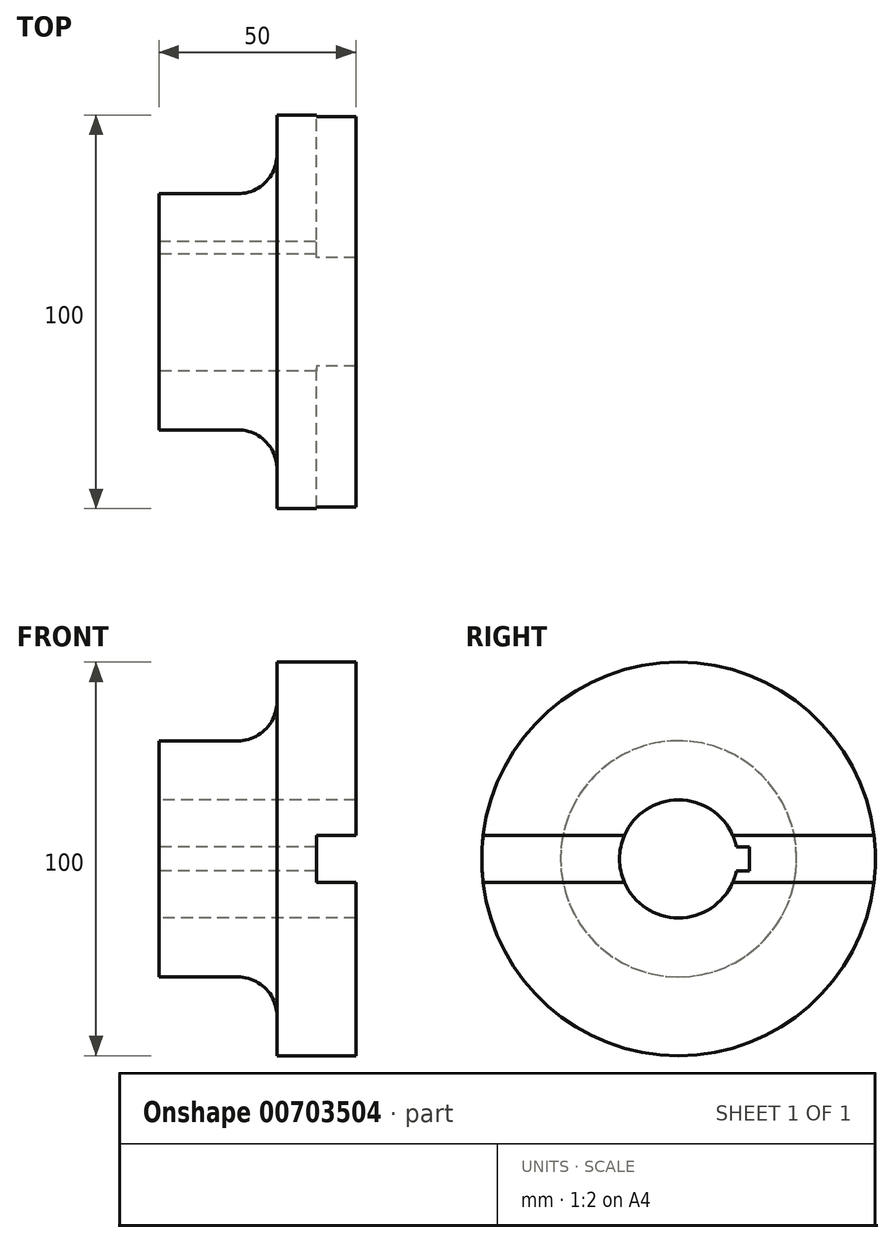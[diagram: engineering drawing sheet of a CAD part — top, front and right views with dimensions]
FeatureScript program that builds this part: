
annotation { "Feature Type Name" : "Feature", "Feature Type Description" : "" }
export const myFeature = defineFeature(function(context is Context, id is Id, definition is map)
    precondition{}
    {
        {
            var Q0;
            Q0=qCreatedBy(makeId("Top.planeOp"),FACE);
            var sketch = newSketch(context, id + "F0", { "sketchPlane" : qUnion([Q0])});
            skLineSegment(sketch, "E0", {"start": v(0, 0) * mm, "end": v(0, 50) * mm});
            skLineSegment(sketch, "E1", {"start": v(0, 50) * mm, "end": v(-20, 50) * mm});
            skLineSegment(sketch, "E2", {"start": v(-20, 50) * mm, "end": v(-20, 30) * mm});
            skLineSegment(sketch, "E3", {"start": v(-20, 30) * mm, "end": v(-50, 30) * mm});
            skLineSegment(sketch, "E4", {"start": v(-50, 30) * mm, "end": v(-50, 0) * mm});
            skLineSegment(sketch, "E5", {"start": v(-50, 0) * mm, "end": v(0, 0) * mm});
            skSolve(sketch);
        }
        {
            var Q0;
            Q0 = qSketchRegion(id + "F0", true);
            var Q1;
            Q1=sQuery(id+"F0.wireOp",EDGE,"E5");
            revolve(context, id + "F1", {"surfaceOperationType" : NewSurfaceOperationType.NEW, "entities" : qUnion([Q0]), "axis" : qUnion([Q1]), "revolveType" : RevolveType.FULL});
        }
        {
            var Q0;
            Q0=makeQuery(id+"F1.opRevolve","SWEPT_FACE",FACE,{"disambiguationData":[OSD([sQuery(id+"F0.wireOp",EDGE,"E0")])]});
            var sketch = newSketch(context, id + "F2", { "sketchPlane" : qUnion([Q0])});
            skLineSegment(sketch, "E6.bottom", {"start": v(-50, 6) * mm, "end": v(50, 6) * mm});
            skLineSegment(sketch, "E6.top", {"start": v(-50, -6) * mm, "end": v(50, -6) * mm});
            skLineSegment(sketch, "E6.left", {"start": v(-50, 6) * mm, "end": v(-50, -6) * mm});
            skLineSegment(sketch, "E6.right", {"start": v(50, 6) * mm, "end": v(50, -6) * mm});
            skPoint(sketch, "E6.middle", {"position": v(0, 0) * mm});
            skSolve(sketch);
        }
        {
            var Q0;
            {var subQ0=sQuery(id+"F2.wireOp",EDGE,"E6.bottom");var subQ1=makeQuery(id+"F1.opRevolve","SWEPT_EDGE",EDGE,{"disambiguationData":[OSD([sQuery(id+"F0.wireOp",EDGE,"E0"),sQuery(id+"F0.wireOp",EDGE,"E1")])]});var subQ4=makeQuery(id+"F2.imprint","INTERSECT",VERTEX,{"disambiguationData":[OD(0.0)],"derivedFrom":[subQ1,subQ0]});Q0=makeQuery(id+"F2.imprint","IMPRINT",FACE,{"disambiguationData":[TD([[makeQuery(id+"F2.imprint","IMPRINT",EDGE,{"disambiguationData":[TD([[subQ4,-1.0]])],"derivedFrom":subQ0}),-1.0]])]});}
            extrude(context, id + "F3", {"entities" : qUnion([Q0]), "operationType" : NewBodyOperationType.REMOVE, "oppositeDirection" : true, "depth" : 10 * mm, "offsetDistance" : 25 * mm});
        }
        {
            var Q0;
            Q0=makeQuery(id+"F1.opRevolve","SWEPT_FACE",FACE,{"disambiguationData":[OSD([sQuery(id+"F0.wireOp",EDGE,"E4")])]});
            var sketch = newSketch(context, id + "F4", { "sketchPlane" : qUnion([Q0])});
            skCircle(sketch, "E7", {"center": v(0, 0) * mm, "radius": 15 * mm});
            skSolve(sketch);
        }
        {
            var Q0;
            Q0=makeQuery(id+"F4.imprint","IMPRINT",FACE,{"disambiguationData":[TD([[makeQuery(id+"F4.imprint","IMPRINT",EDGE,{"derivedFrom":sQuery(id+"F4.wireOp",EDGE,"E7")}),1.0]])]});
            extrude(context, id + "F5", {"entities" : qUnion([Q0]), "operationType" : NewBodyOperationType.REMOVE, "oppositeDirection" : true, "depth" : 52.4 * mm, "offsetDistance" : 25 * mm});
        }
        {
            var Q0;
            Q0=qCreatedBy(makeId("Front.planeOp"),FACE);
            var sketch = newSketch(context, id + "F6", { "sketchPlane" : qUnion([Q0])});
            skLineSegment(sketch, "E8.bottom", {"start": v(-50, -3) * mm, "end": v(50, -3) * mm});
            skLineSegment(sketch, "E8.top", {"start": v(-50, 3) * mm, "end": v(50, 3) * mm});
            skLineSegment(sketch, "E8.left", {"start": v(-50, -3) * mm, "end": v(-50, 3) * mm});
            skLineSegment(sketch, "E8.right", {"start": v(50, -3) * mm, "end": v(50, 3) * mm});
            skPoint(sketch, "E8.middle", {"position": v(0, 0) * mm});
            skSolve(sketch);
        }
        {
            var Q0;
            Q0 = qSketchRegion(id + "F6", true);
            extrude(context, id + "F7", {"entities" : qUnion([Q0]), "operationType" : NewBodyOperationType.REMOVE, "oppositeDirection" : true, "depth" : 18 * mm, "offsetDistance" : 25 * mm});
        }
        {
            var Q0;
            Q0=makeQuery(id+"F1.opRevolve","SWEPT_EDGE",EDGE,{"disambiguationData":[OSD([sQuery(id+"F0.wireOp",EDGE,"E2"),sQuery(id+"F0.wireOp",EDGE,"E3")])]});
            fillet(context, id + "F8", {"entities" : qUnion([Q0]), "radius" : 10 * mm, "tangentPropagation" : true, "allowEdgeOverflow" : false});
        }
    });
